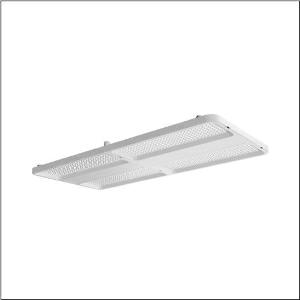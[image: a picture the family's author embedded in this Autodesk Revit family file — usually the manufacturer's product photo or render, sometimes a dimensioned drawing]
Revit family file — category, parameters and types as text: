
# Revit family: highbay_21_maxi_52hn11db4mea
name_source: partatom
category: Lighting Fixtures
units: mm (PartAtom-declared; Revit-internal decimal feet)

## family parameters
Cut with Voids When Loaded = No
Host = Face
Light Source = No
Part Type = Normal
Room Calculation Point = No
Round Connector Dimension = Use Diameter
Shared = No

## types (1)
- --- (1 x LED, 4230 lm, 22.6 W, 4000K)
    Apparent Load = 23 VA
    CIE Flux Codes = 89 97 99 100 100
    Color Rendering = 80
    Color Temperature = 4000K
    Default Elevation = 1800 mm
    Description = high bay luminaire Highbay 21 maxi; direct symmetric narrow distribution, light control with lens of PMMA; UGR ≤ 19 (X = 4H | Y = 8H | S = 0.25H | reflection values 70/50/20); luminous flux: 28.000lm; light colour: 840, colour temperature: 4000K, MacAdam ≤ 3 SDCM (initial), colour rendering: CRI > 80; luminous efficacy: 194,4lm/W; rated service life: 75.000h (L80) at AT= ta max; control: DALI 2; luminaire connection: 2x terminal, 5-pole, max. 2.5mm² with through-wiring: 1x feed-in / 1x feed-out (cable entry for two cables, Ø 8.5..13mm); mains connection: 230..240V, AC/DC 0/50..60Hz; connected load: 144W; protection rating (complete): IP66; insulation class (complete): insulation class I (protective earthing); protection symbol: D; impact resistance: IK08; certification: CE, ENEC, VDE, UKCA; luminaire for central battery installations according to EN 60598-2-22, internal wiring halogen-free; luminaire LABS conformity tested according to VDMA 24364:2018-05; Suitable for use in the food industry according to the specifications of IFS-Food, HACCP and/or BRC; housing frame of high-performance plastic PA6, matt traffic white (RAL 9016); cover of PMMA; dimension (LxWxH): 946 x 442 x 72mm; permissible operating ambient temperature: -40..+65°C (reducing of maximum allowable ambient temperature of 5°C with ceiling mounting); packaging unit: 1 piece; (delivery without accessories; please order mounting accessories separately)
    Height = 72 mm  [stored 0.23622 ft]
    Lamp = 1 x LED
    Lamp Light Flux = 4230 lm
    Lamp Power = 22.6 W
    Lamp count = 1
    Length = 946 mm
    Luminous efficacy = 187 lm/W
    Manufacturer = Siteco
    ModVariant = No
    Model = 52HN11DB4MEA
    Mounting Place = Ceiling
    Mounting Type = Pendant
    Number of Poles = 1
    OnlyDefault = Yes
    Power Factor = 1
    Product Name = Highbay 21 maxi
    Product group = high bay luminaire
    ProductGroupID = 902
    Protection Class = Protection class I
    Protection Degree = IP 66
    RLX_Detail_Level = 1
    RLX_Emergency_Light_Flux = 0 lm
    RLX_Emergency_Type = 0
    RLX_Emergency_Type_DB = No
    RlxData = <blob elided: 128345 chars, md5=63e88108>
    Socket = socket
    Standby Power = 0 W
    System Light Flux = 4230 lm
    System Power = 23 W
    Type Comments = : DC mode (central or group accumulator) initial emergency light level
    Type Image = l_1363244.jpg
    URL = http://relux.com
    VarID = @adj_017775
    Voltage = 0 V
    Weight = 0.00 kg
    Width = 442 mm

note: [stored X ft] marks values corroborated as IEEE doubles in the binary element streams (Revit-internal decimal feet)

## geometry (parser evidence)
native form markers: Blend x4, Sweep x11
no freeform markers — native parametric forms only
